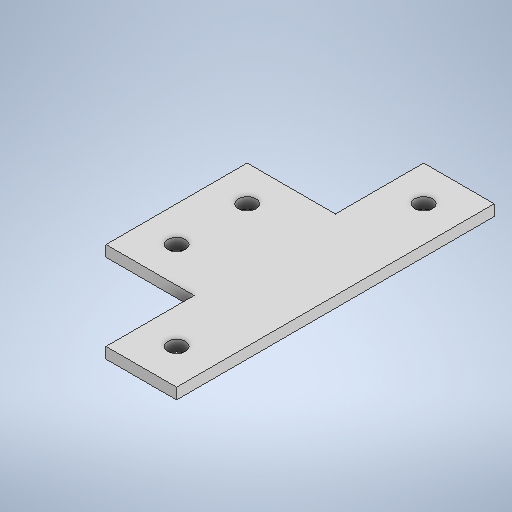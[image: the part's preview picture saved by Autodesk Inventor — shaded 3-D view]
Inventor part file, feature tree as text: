
AUTODESK INVENTOR PART (.ipt)
format: ipt  version: 2025.1 (Build 291241000, 241)  size: 250,880 bytes
history: native  units: in
note: dims shown in document units (in); Inventor stores cm internally (conversion verified against a paired STEP export)
features: extrude x1, sketch x1
ambient origin geometry x8: Origin, YZ Plane, XZ Plane, XY Plane, X Axis, Y Axis, Z Axis, Center Point
bodies: Solid1 (feature_tree)
feature tree (2):
  extrude  "Extrusion1"  Depth=1.6in
  sketch  "Sketch1"  dims[d0=1.0in d1=1.6in d2=0.4in d3=0.4in d4=90.0deg d5=0.4in d6=0.4in d7=90.0deg d8=0.2in d9=0.2in d10=1.0in d11=90.0deg d12=0.8in d13=3.6in d14=90.0deg d15=0.8in d16=90.0deg d17=0.4in d18=90.0deg d19=0.4in d20=90.0deg d21=0.2in d22=0.2in d23=0.125in d24=0.0in]
